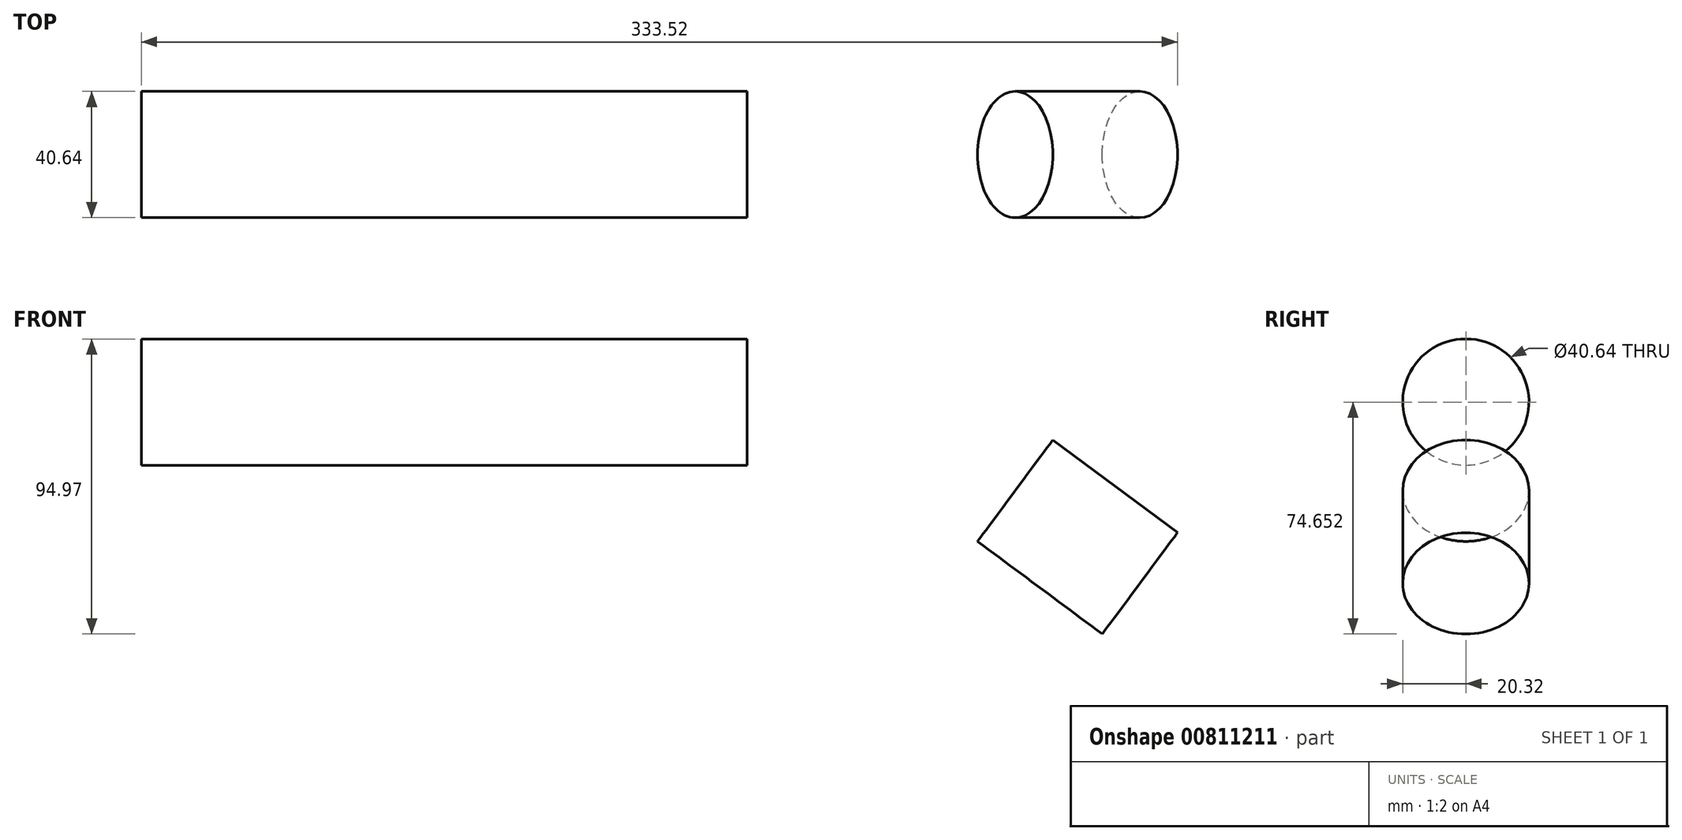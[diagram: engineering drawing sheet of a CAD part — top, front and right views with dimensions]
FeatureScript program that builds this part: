
annotation { "Feature Type Name" : "Feature", "Feature Type Description" : "" }
export const myFeature = defineFeature(function(context is Context, id is Id, definition is map)
    precondition{}
    {
        {
            var Q0;
            Q0=qCreatedBy(makeId("Front.planeOp"),FACE);
            var sketch = newSketch(context, id + "F0", { "sketchPlane" : qUnion([Q0])});
            skLineSegment(sketch, "E0", {"start": v(-186, 20.92) * mm, "end": v(9, 20.92) * mm});
            skArc(sketch, "E1", {"start": v(107.37, -11.61) * mm, "mid": v(60.8, 12.58) * mm, "end": v(9, 20.92) * mm});
            skLineSegment(sketch, "E2", {"start": v(107.37, -11.61) * mm, "end": v(147.51, -41.42) * mm});
            skLineSegment(sketch, "E3.0", {"start": v(95.25, -27.92) * mm, "end": v(135.4, -57.74) * mm});
            skArc(sketch, "E3.1", {"start": v(95.25, -27.92) * mm, "mid": v(54.42, -6.71) * mm, "end": v(9, 0.6) * mm});
            skLineSegment(sketch, "E3.2", {"start": v(-186, 0.6) * mm, "end": v(9, 0.6) * mm});
            skSolve(sketch);
        }
        {
            var Q0;
            Q0=sQuery(id+"F0.wireOp",EDGE,"E0");
            var Q1;
            Q1=sQuery(id+"F0.wireOp",EDGE,"E3.2");
            revolve(context, id + "F1", {"bodyType" : ToolBodyType.SURFACE, "surfaceOperationType" : NewSurfaceOperationType.NEW, "surfaceEntities" : qUnion([Q0]), "axis" : qUnion([Q1]), "revolveType" : RevolveType.FULL});
        }
        {
            var Q0;
            Q0=sQuery(id+"F0.wireOp",EDGE,"E2");
            var Q1;
            Q1=sQuery(id+"F0.wireOp",EDGE,"E3.0");
            revolve(context, id + "F2", {"bodyType" : ToolBodyType.SURFACE, "surfaceOperationType" : NewSurfaceOperationType.NEW, "surfaceEntities" : qUnion([Q0]), "axis" : qUnion([Q1]), "revolveType" : RevolveType.FULL});
        }
    });
